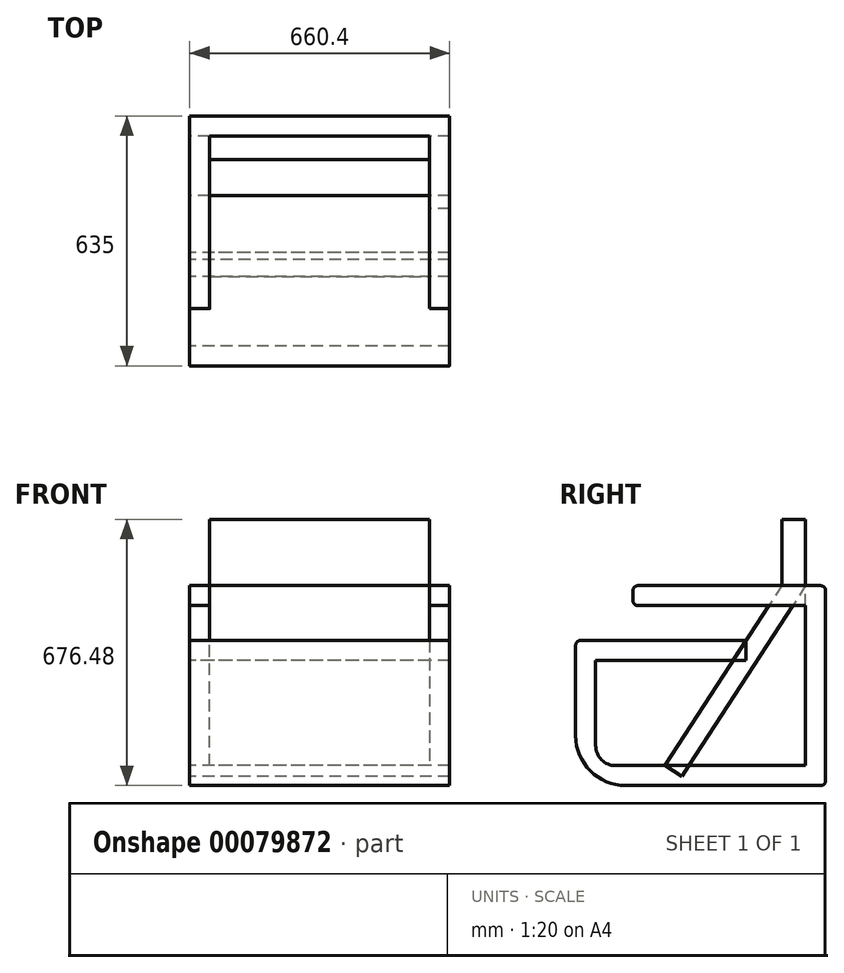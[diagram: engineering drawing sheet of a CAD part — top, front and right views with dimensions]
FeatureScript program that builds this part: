
annotation { "Feature Type Name" : "Feature", "Feature Type Description" : "" }
export const myFeature = defineFeature(function(context is Context, id is Id, definition is map)
    precondition{}
    {
        {
            var Q0;
            Q0=qCreatedBy(makeId("Right.planeOp"),FACE);
            var sketch = newSketch(context, id + "F0", { "sketchPlane" : qUnion([Q0])});
            skLineSegment(sketch, "E0.bottom", {"start": v(-310.8, 0) * mm, "end": v(324.2, 0) * mm, "construction": true});
            skLineSegment(sketch, "E0.top", {"start": v(-310.8, 508) * mm, "end": v(324.2, 508) * mm, "construction": true});
            skLineSegment(sketch, "E0.left", {"start": v(-310.8, 0) * mm, "end": v(-310.8, 508) * mm, "construction": true});
            skLineSegment(sketch, "E0.right", {"start": v(324.2, 0) * mm, "end": v(324.2, 508) * mm, "construction": true});
            skLineSegment(sketch, "E1", {"start": v(324.2, 508) * mm, "end": v(324.2, 0) * mm});
            skLineSegment(sketch, "E2", {"start": v(-310.8, 127) * mm, "end": v(-310.8, 368.78) * mm});
            skLineSegment(sketch, "E3", {"start": v(-310.8, 368.78) * mm, "end": v(121.98, 368.78) * mm});
            skLineSegment(sketch, "E4", {"start": v(121.98, 368.78) * mm, "end": v(121.98, 317.98) * mm});
            skLineSegment(sketch, "E5", {"start": v(121.98, 317.98) * mm, "end": v(-260, 317.98) * mm});
            skLineSegment(sketch, "E6", {"start": v(-260, 317.98) * mm, "end": v(-260, 101.6) * mm});
            skLineSegment(sketch, "E7", {"start": v(-209.2, 50.8) * mm, "end": v(273.4, 50.8) * mm});
            skLineSegment(sketch, "E8", {"start": v(273.4, 50.8) * mm, "end": v(273.4, 457.2) * mm});
            skLineSegment(sketch, "E9", {"start": v(273.4, 457.2) * mm, "end": v(-165.46, 457.2) * mm});
            skLineSegment(sketch, "E10", {"start": v(-165.46, 457.2) * mm, "end": v(-165.46, 508) * mm});
            skLineSegment(sketch, "E11", {"start": v(-165.46, 508) * mm, "end": v(324.2, 508) * mm});
            skPoint(sketch, "E12.visualSharp", {"position": v(-260, 50.8) * mm});
            skArc(sketch, "E12.filletArc", {"start": v(-260, 101.6) * mm, "mid": v(-245.11, 65.68) * mm, "end": v(-209.2, 50.8) * mm});
            skLineSegment(sketch, "E13", {"start": v(324.2, 0) * mm, "end": v(-183.8, 0) * mm});
            skPoint(sketch, "E14.visualSharp", {"position": v(-310.8, 0) * mm});
            skArc(sketch, "E14.filletArc", {"start": v(-310.8, 127) * mm, "mid": v(-273.6, 37.2) * mm, "end": v(-183.8, 0) * mm});
            skSolve(sketch);
        }
        {
            var Q0;
            Q0 = qSketchRegion(id + "F0", true);
            extrude(context, id + "F1", {"entities" : qUnion([Q0]), "depth" : 660.4 * mm});
        }
        {
            var Q0;
            Q0=makeQuery(id+"F1.opExtrude","SWEPT_FACE",FACE,{"disambiguationData":[OSD([sQuery(id+"F0.wireOp",EDGE,"E11")])]});
            var sketch = newSketch(context, id + "F2", { "sketchPlane" : qUnion([Q0])});
            skLineSegment(sketch, "E15.0", {"start": v(50.8, -114.66) * mm, "end": v(50.8, 273.4) * mm});
            skLineSegment(sketch, "E15.2", {"start": v(609.6, -114.66) * mm, "end": v(609.6, 273.4) * mm});
            skLineSegment(sketch, "E15.3", {"start": v(609.6, 273.4) * mm, "end": v(50.8, 273.4) * mm});
            skLineSegment(sketch, "E16", {"start": v(50.8, -114.66) * mm, "end": v(50.8, -165.46) * mm});
            skLineSegment(sketch, "E17", {"start": v(609.6, -114.66) * mm, "end": v(609.6, -165.46) * mm});
            skLineSegment(sketch, "E18", {"start": v(50.8, -165.46) * mm, "end": v(609.6, -165.46) * mm});
            skSolve(sketch);
        }
        {
            var Q0;
            Q0 = qSketchRegion(id + "F2", true);
            extrude(context, id + "F3", {"entities" : qUnion([Q0]), "operationType" : NewBodyOperationType.REMOVE, "oppositeDirection" : true, "depth" : 86.54 * mm});
        }
        {
            var Q0;
            Q0=makeQuery(id+"F3.boolean.opBoolean","COPY",FACE,{"derivedFrom":makeQuery(id+"F3.opExtrude","SWEPT_FACE",FACE,{"disambiguationData":[OSD([sQuery(id+"F2.wireOp",EDGE,"E15.2"),sQuery(id+"F2.wireOp",EDGE,"E17")])]})});
            var sketch = newSketch(context, id + "F4", { "sketchPlane" : qUnion([Q0])});
            skLineSegment(sketch, "E19", {"start": v(-273.4, 508) * mm, "end": v(41.3, 23.14) * mm});
            skLineSegment(sketch, "E20", {"start": v(-212.84, 508) * mm, "end": v(83.92, 50.8) * mm});
            skLineSegment(sketch, "E21", {"start": v(83.92, 50.8) * mm, "end": v(41.3, 23.14) * mm});
            skLineSegment(sketch, "E22.top", {"start": v(-273.4, 676.48) * mm, "end": v(-212.84, 676.48) * mm});
            skLineSegment(sketch, "E22.left", {"start": v(-273.4, 508) * mm, "end": v(-273.4, 676.48) * mm});
            skLineSegment(sketch, "E22.right", {"start": v(-212.84, 508) * mm, "end": v(-212.84, 676.48) * mm});
            skSolve(sketch);
        }
        {
            var Q0;
            Q0 = qSketchRegion(id + "F4", true);
            var Q1;
            Q1=makeQuery(id+"F3.boolean.opBoolean","COPY",FACE,{"derivedFrom":makeQuery(id+"F3.opExtrude","SWEPT_FACE",FACE,{"disambiguationData":[OSD([sQuery(id+"F2.wireOp",EDGE,"E15.0"),sQuery(id+"F2.wireOp",EDGE,"E16")])]})});
            extrude(context, id + "F5", {"entities" : qUnion([Q0]), "endBound" : BoundingType.UP_TO_SURFACE, "endBoundEntityFace" : qUnion([Q1]), "depth" : 25.4 * mm});
        }
        {
            var Q0;
            Q0=makeQuery(id+"F1.opExtrude","CAP_FACE",FACE,{"disambiguationData":[OSD([sQuery(id+"F0.wireOp",EDGE,"E1"),sQuery(id+"F0.wireOp",EDGE,"E2"),sQuery(id+"F0.wireOp",EDGE,"E3"),sQuery(id+"F0.wireOp",EDGE,"E4"),sQuery(id+"F0.wireOp",EDGE,"E5"),sQuery(id+"F0.wireOp",EDGE,"E6"),sQuery(id+"F0.wireOp",EDGE,"E7"),sQuery(id+"F0.wireOp",EDGE,"E8"),sQuery(id+"F0.wireOp",EDGE,"E9"),sQuery(id+"F0.wireOp",EDGE,"E10"),sQuery(id+"F0.wireOp",EDGE,"E11"),sQuery(id+"F0.wireOp",EDGE,"E12.filletArc"),sQuery(id+"F0.wireOp",EDGE,"E13"),sQuery(id+"F0.wireOp",EDGE,"E14.filletArc")])],"isStart":true});
            var sketch = newSketch(context, id + "F6", { "sketchPlane" : qUnion([Q0])});
            skLineSegment(sketch, "E23.0", {"start": v(41.3, 23.14) * mm, "end": v(23.35, 50.8) * mm});
            skLineSegment(sketch, "E24", {"start": v(83.92, 50.8) * mm, "end": v(41.3, 23.14) * mm});
            skLineSegment(sketch, "E25", {"start": v(83.92, 50.8) * mm, "end": v(23.35, 50.8) * mm});
            skPoint(sketch, "E26.orphan", {"position": v(-273.4, 508) * mm});
            skPoint(sketch, "E23.1.end.orphan", {"position": v(-212.84, 508) * mm});
            skSolve(sketch);
        }
        {
            var Q0;
            Q0 = qSketchRegion(id + "F6", true);
            extrude(context, id + "F7", {"entities" : qUnion([Q0]), "operationType" : NewBodyOperationType.REMOVE, "oppositeDirection" : true, "depth" : 762 * mm});
        }
        {
            var Q0;
            Q0=makeQuery(id+"F1.opExtrude","SWEPT_EDGE",EDGE,{"disambiguationData":[OSD([sQuery(id+"F0.wireOp",EDGE,"E1"),sQuery(id+"F0.wireOp",EDGE,"E13")])]});
            var Q1;
            Q1=makeQuery(id+"F1.opExtrude","SWEPT_EDGE",EDGE,{"disambiguationData":[OSD([sQuery(id+"F0.wireOp",EDGE,"E1"),sQuery(id+"F0.wireOp",EDGE,"E11")])]});
            var Q2;
            {var subQ0=sQuery(id+"F0.wireOp",EDGE,"E11");var subQ1=sQuery(id+"F0.wireOp",EDGE,"E10");Q2=makeQuery(id+"F3.boolean.opBoolean","SPLIT",EDGE,{"disambiguationData":[TD([makeQuery(id+"F3.opExtrude","SWEPT_FACE",FACE,{"disambiguationData":[OSD([sQuery(id+"F2.wireOp",EDGE,"E15.0"),sQuery(id+"F2.wireOp",EDGE,"E16")])]})])],"derivedFrom":makeQuery(id+"F1.opExtrude","SWEPT_EDGE",EDGE,{"disambiguationData":[OSD([subQ1,subQ0])]})});}
            var Q3;
            {var subQ0=sQuery(id+"F0.wireOp",EDGE,"E10");var subQ1=sQuery(id+"F0.wireOp",EDGE,"E9");Q3=makeQuery(id+"F3.boolean.opBoolean","SPLIT",EDGE,{"disambiguationData":[TD([makeQuery(id+"F3.opExtrude","SWEPT_FACE",FACE,{"disambiguationData":[OSD([sQuery(id+"F2.wireOp",EDGE,"E15.0"),sQuery(id+"F2.wireOp",EDGE,"E16")])]})])],"derivedFrom":makeQuery(id+"F1.opExtrude","SWEPT_EDGE",EDGE,{"disambiguationData":[OSD([subQ1,subQ0])]})});}
            var Q4;
            {var subQ0=sQuery(id+"F0.wireOp",EDGE,"E11");var subQ1=sQuery(id+"F0.wireOp",EDGE,"E10");Q4=makeQuery(id+"F3.boolean.opBoolean","SPLIT",EDGE,{"disambiguationData":[TD([makeQuery(id+"F3.opExtrude","SWEPT_FACE",FACE,{"disambiguationData":[OSD([sQuery(id+"F2.wireOp",EDGE,"E15.2"),sQuery(id+"F2.wireOp",EDGE,"E17")])]})])],"derivedFrom":makeQuery(id+"F1.opExtrude","SWEPT_EDGE",EDGE,{"disambiguationData":[OSD([subQ1,subQ0])]})});}
            var Q5;
            {var subQ0=sQuery(id+"F0.wireOp",EDGE,"E10");var subQ1=sQuery(id+"F0.wireOp",EDGE,"E9");Q5=makeQuery(id+"F3.boolean.opBoolean","SPLIT",EDGE,{"disambiguationData":[TD([makeQuery(id+"F3.opExtrude","SWEPT_FACE",FACE,{"disambiguationData":[OSD([sQuery(id+"F2.wireOp",EDGE,"E15.2"),sQuery(id+"F2.wireOp",EDGE,"E17")])]})])],"derivedFrom":makeQuery(id+"F1.opExtrude","SWEPT_EDGE",EDGE,{"disambiguationData":[OSD([subQ1,subQ0])]})});}
            var Q6;
            Q6=makeQuery(id+"F1.opExtrude","SWEPT_EDGE",EDGE,{"disambiguationData":[OSD([sQuery(id+"F0.wireOp",EDGE,"E2"),sQuery(id+"F0.wireOp",EDGE,"E3")])]});
            fillet(context, id + "F8", {"entities" : qUnion([Q0, Q1, Q2, Q3, Q4, Q5, Q6]), "radius" : 12.7 * mm, "tangentPropagation" : true, "allowEdgeOverflow" : false});
        }
        {
            var Q0;
            {var subQ0=sQuery(id+"F4.wireOp",EDGE,"E21");Q0=makeQuery(id+"F4.imprint","IMPRINT",FACE,{"disambiguationData":[TD([[makeQuery(id+"F4.imprint","IMPRINT",EDGE,{"derivedFrom":subQ0}),-1.0]])]});}
            var sketch = newSketch(context, id + "F9", { "sketchPlane" : qUnion([Q0])});
            skLineSegment(sketch, "E27.0", {"start": v(-121.98, 368.78) * mm, "end": v(-121.98, 317.98) * mm});
            skLineSegment(sketch, "E27.1", {"start": v(-121.98, 317.98) * mm, "end": v(-89.1, 317.98) * mm});
            skLineSegment(sketch, "E28", {"start": v(-121.98, 368.78) * mm, "end": v(-89.1, 317.98) * mm});
            skPoint(sketch, "E29.orphan", {"position": v(260, 317.98) * mm});
            skSolve(sketch);
        }
        {
            var Q0;
            Q0 = qSketchRegion(id + "F9", true);
            extrude(context, id + "F10", {"entities" : qUnion([Q0]), "operationType" : NewBodyOperationType.REMOVE, "oppositeDirection" : true, "depth" : 762 * mm});
        }
    });
